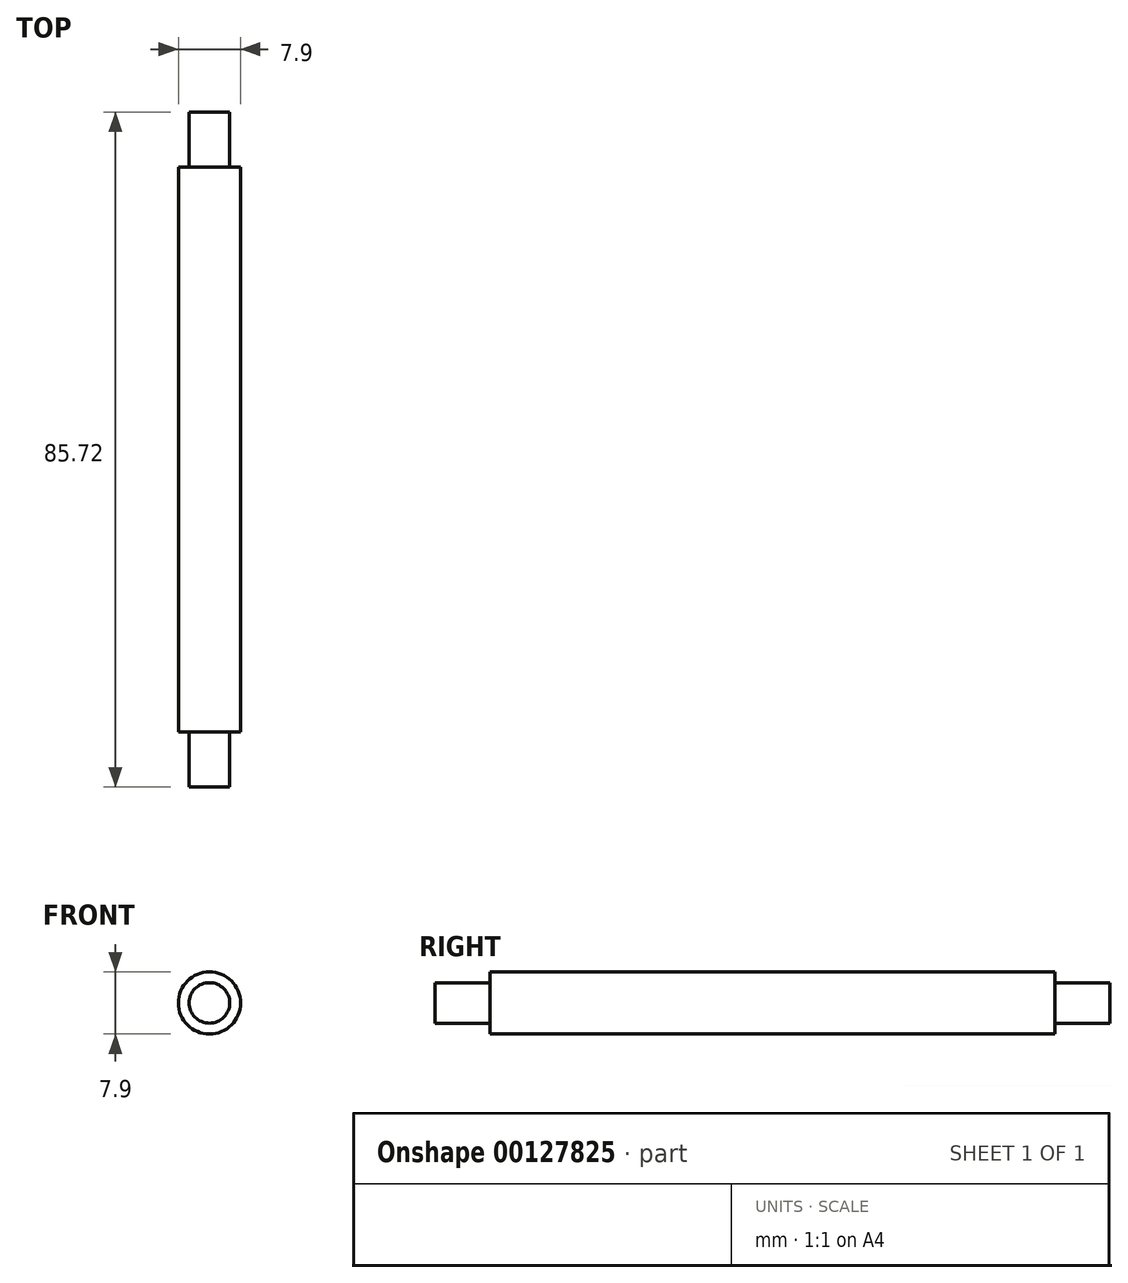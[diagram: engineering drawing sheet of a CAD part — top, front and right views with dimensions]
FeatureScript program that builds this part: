
annotation { "Feature Type Name" : "Feature", "Feature Type Description" : "" }
export const myFeature = defineFeature(function(context is Context, id is Id, definition is map)
    precondition{}
    {
        {
            var Q0;
            Q0=qCreatedBy(makeId("Front.planeOp"),FACE);
            var sketch = newSketch(context, id + "F0", { "sketchPlane" : qUnion([Q0])});
            skCircle(sketch, "E0", {"center": v(0, 0) * mm, "radius": 3.95 * mm});
            skSolve(sketch);
        }
        {
            var Q0;
            Q0 = qSketchRegion(id + "F0", true);
            extrude(context, id + "F1", {"entities" : qUnion([Q0]), "depth" : 35.86 * mm, "hasSecondDirection" : true, "secondDirectionOppositeDirection" : true, "secondDirectionDepth" : 35.86 * mm});
        }
        {
            var Q0;
            Q0=makeQuery(id+"F1.opExtrude","CAP_FACE",FACE,{"disambiguationData":[OSD([sQuery(id+"F0.wireOp",EDGE,"E0")])],"isStart":false});
            var sketch = newSketch(context, id + "F2", { "sketchPlane" : qUnion([Q0])});
            skCircle(sketch, "E1", {"center": v(0, 0) * mm, "radius": 2.58 * mm});
            skSolve(sketch);
        }
        {
            var Q0;
            Q0 = qSketchRegion(id + "F2", true);
            extrude(context, id + "F3", {"entities" : qUnion([Q0]), "operationType" : NewBodyOperationType.ADD, "depth" : 7 * mm});
        }
        {
            var Q0;
            Q0=makeQuery(id+"F1.opExtrude","CAP_FACE",FACE,{"disambiguationData":[OSD([sQuery(id+"F0.wireOp",EDGE,"E0")])],"isStart":true});
            var sketch = newSketch(context, id + "F4", { "sketchPlane" : qUnion([Q0])});
            skCircle(sketch, "E2", {"center": v(0, 0) * mm, "radius": 2.58 * mm});
            skSolve(sketch);
        }
        {
            var Q0;
            Q0 = qSketchRegion(id + "F4", true);
            extrude(context, id + "F5", {"entities" : qUnion([Q0]), "operationType" : NewBodyOperationType.ADD, "depth" : 7 * mm});
        }
    });
